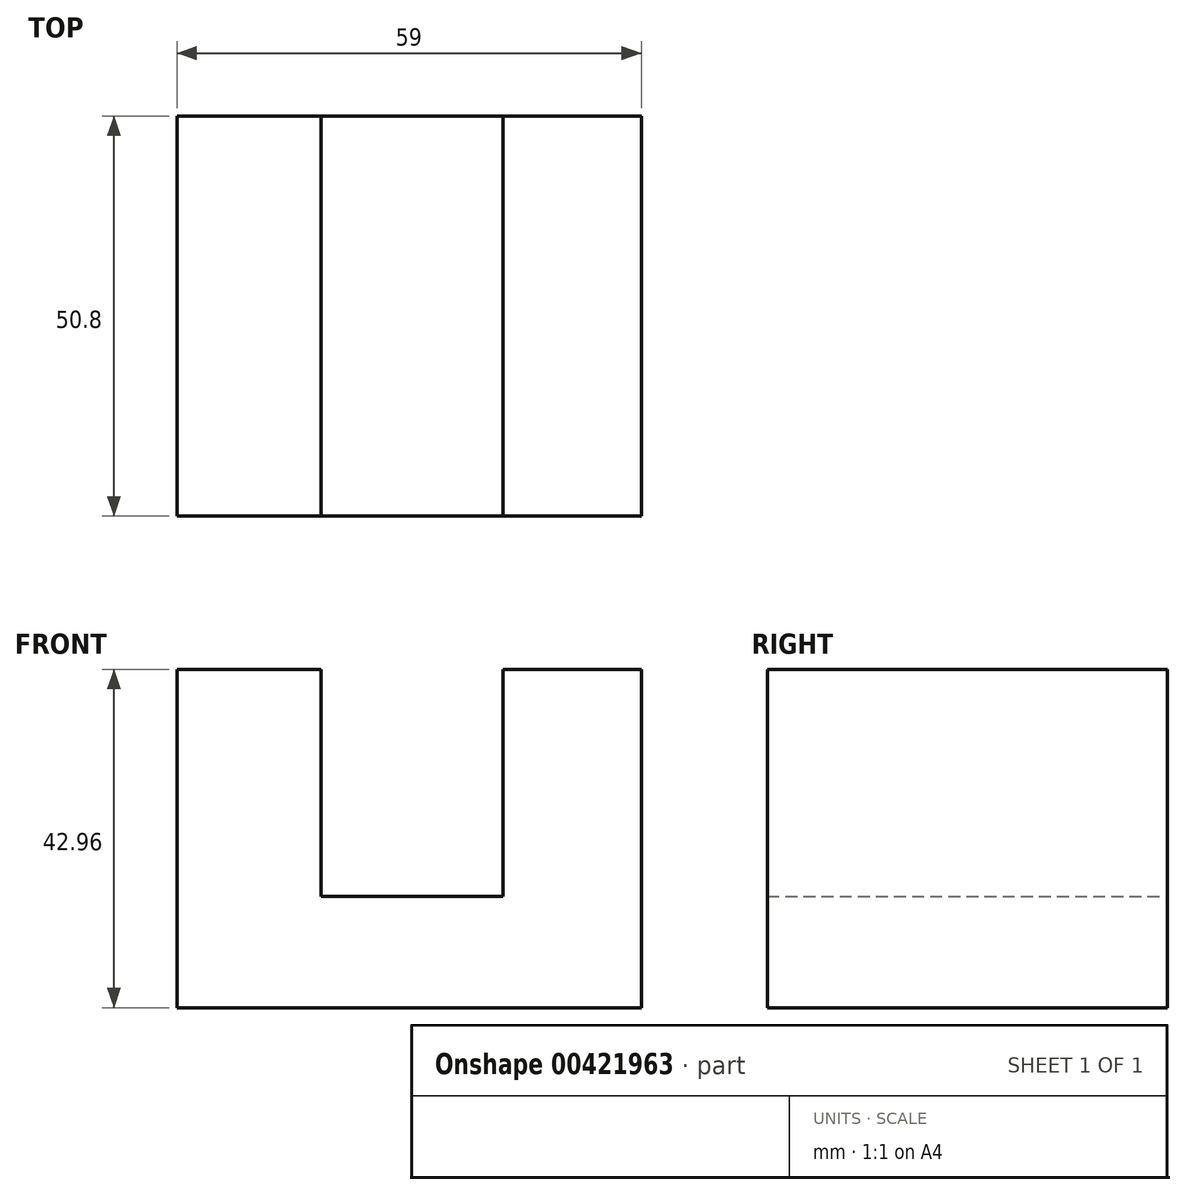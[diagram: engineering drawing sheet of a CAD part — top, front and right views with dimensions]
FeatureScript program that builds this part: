
annotation { "Feature Type Name" : "Feature", "Feature Type Description" : "" }
export const myFeature = defineFeature(function(context is Context, id is Id, definition is map)
    precondition{}
    {
        {
            var Q0;
            Q0=qCreatedBy(makeId("Front.planeOp"),FACE);
            var sketch = newSketch(context, id + "F0", { "sketchPlane" : qUnion([Q0])});
            skLineSegment(sketch, "E0", {"start": v(0, 42.96) * mm, "end": v(0, 0) * mm});
            skLineSegment(sketch, "E1", {"start": v(0, 0) * mm, "end": v(-59, 0) * mm});
            skLineSegment(sketch, "E2", {"start": v(-59, 0) * mm, "end": v(-59, 42.96) * mm});
            skLineSegment(sketch, "E3", {"start": v(-59, 42.96) * mm, "end": v(-40.67, 42.96) * mm});
            skLineSegment(sketch, "E4", {"start": v(-40.67, 42.96) * mm, "end": v(-40.67, 14.13) * mm});
            skLineSegment(sketch, "E5", {"start": v(-40.67, 14.13) * mm, "end": v(-17.57, 14.13) * mm});
            skLineSegment(sketch, "E6", {"start": v(-17.57, 14.13) * mm, "end": v(-17.57, 42.96) * mm});
            skLineSegment(sketch, "E7", {"start": v(-17.57, 42.96) * mm, "end": v(0, 42.96) * mm});
            skSolve(sketch);
        }
        {
            var Q0;
            Q0=makeQuery(id+"F0.imprint","IMPRINT",FACE,{"disambiguationData":[TD([[makeQuery(id+"F0.imprint","IMPRINT",EDGE,{"derivedFrom":sQuery(id+"F0.wireOp",EDGE,"E0")}),-1.0]])]});
            extrude(context, id + "F1", {"entities" : qUnion([Q0]), "depth" : 50.8 * mm});
        }
    });
